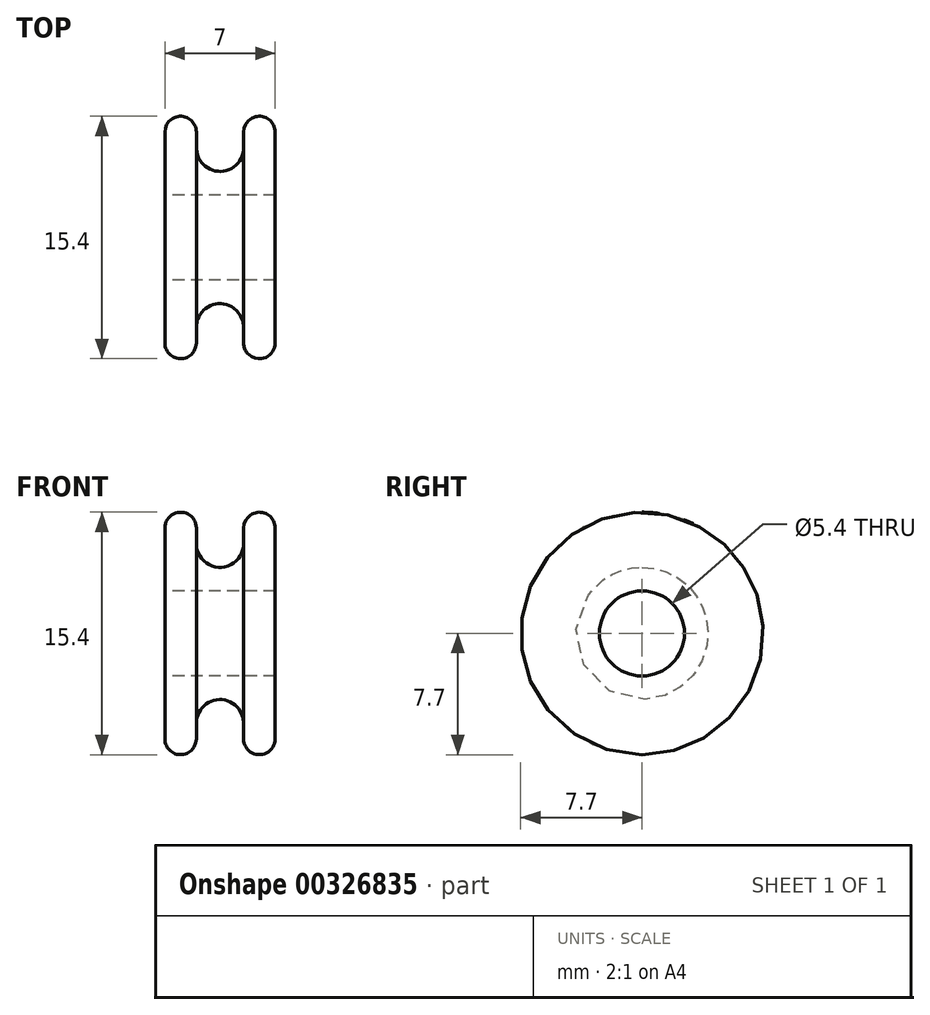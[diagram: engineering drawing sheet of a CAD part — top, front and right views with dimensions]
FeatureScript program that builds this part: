
annotation { "Feature Type Name" : "Feature", "Feature Type Description" : "" }
export const myFeature = defineFeature(function(context is Context, id is Id, definition is map)
    precondition{}
    {
        {
            var Q0;
            Q0=qCreatedBy(makeId("Front.planeOp"),FACE);
            var sketch = newSketch(context, id + "F0", { "sketchPlane" : qUnion([Q0])});
            skLineSegment(sketch, "E0", {"start": v(0, 0) * mm, "end": v(7, 0) * mm});
            skLineSegment(sketch, "E1", {"start": v(0, 0) * mm, "end": v(0, 2.7) * mm});
            skLineSegment(sketch, "E2", {"start": v(0, 2.7) * mm, "end": v(7, 2.7) * mm});
            skLineSegment(sketch, "E3", {"start": v(7, 2.7) * mm, "end": v(7, 0) * mm});
            skLineSegment(sketch, "E4", {"start": v(0, 2.7) * mm, "end": v(0, 7.7) * mm});
            skLineSegment(sketch, "E5", {"start": v(0, 7.7) * mm, "end": v(7, 7.7) * mm});
            skLineSegment(sketch, "E6", {"start": v(7, 7.7) * mm, "end": v(7, 2.7) * mm});
            skLineSegment(sketch, "E7", {"start": v(3.5, 7.7) * mm, "end": v(3.5, 5.7) * mm});
            skCircle(sketch, "E8", {"center": v(3.5, 5.7) * mm, "radius": 1.5 * mm});
            skLineSegment(sketch, "E9", {"start": v(3.5, 5.7) * mm, "end": v(2, 5.7) * mm});
            skLineSegment(sketch, "E10", {"start": v(2, 5.7) * mm, "end": v(2, 7.7) * mm});
            skLineSegment(sketch, "E11", {"start": v(3.5, 5.7) * mm, "end": v(5, 5.7) * mm});
            skLineSegment(sketch, "E12", {"start": v(5, 5.7) * mm, "end": v(5, 7.7) * mm});
            skSolve(sketch);
        }
        {
            var Q0;
            Q0=makeQuery(id+"F0.imprint","IMPRINT",FACE,{"disambiguationData":[TD([[makeQuery(id+"F0.imprint","IMPRINT",EDGE,{"derivedFrom":sQuery(id+"F0.wireOp",EDGE,"E2")}),1.0]])]});
            var Q1;
            Q1=sQuery(id+"F0.wireOp",EDGE,"E0");
            revolve(context, id + "F1", {"entities" : qUnion([Q0]), "axis" : qUnion([Q1]), "revolveType" : RevolveType.FULL});
        }
        {
            var Q0;
            Q0=makeQuery(id+"F1.opRevolve","SWEPT_EDGE",EDGE,{"disambiguationData":[OSD([sQuery(id+"F0.wireOp",EDGE,"E5"),sQuery(id+"F0.wireOp",EDGE,"E6")])]});
            var Q1;
            Q1=makeQuery(id+"F1.opRevolve","SWEPT_EDGE",EDGE,{"disambiguationData":[OSD([sQuery(id+"F0.wireOp",EDGE,"E5"),sQuery(id+"F0.wireOp",EDGE,"E12")])]});
            var Q2;
            Q2=makeQuery(id+"F1.opRevolve","SWEPT_EDGE",EDGE,{"disambiguationData":[OSD([sQuery(id+"F0.wireOp",EDGE,"E5"),sQuery(id+"F0.wireOp",EDGE,"E10")])]});
            var Q3;
            Q3=makeQuery(id+"F1.opRevolve","SWEPT_EDGE",EDGE,{"disambiguationData":[OSD([sQuery(id+"F0.wireOp",EDGE,"E4"),sQuery(id+"F0.wireOp",EDGE,"E5")])]});
            fillet(context, id + "F2", {"entities" : qUnion([Q0, Q1, Q2, Q3]), "radius" : 1 * mm, "tangentPropagation" : true, "allowEdgeOverflow" : false});
        }
    });
